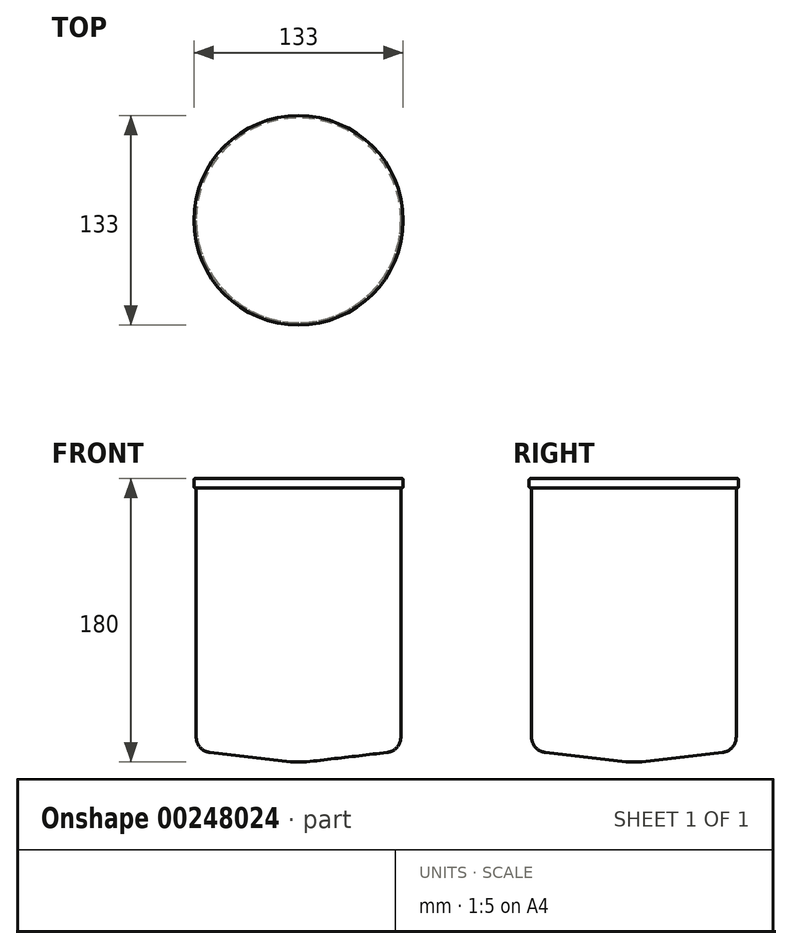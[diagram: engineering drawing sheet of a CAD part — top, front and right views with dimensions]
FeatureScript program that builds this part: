
annotation { "Feature Type Name" : "Feature", "Feature Type Description" : "" }
export const myFeature = defineFeature(function(context is Context, id is Id, definition is map)
    precondition{}
    {
        {
            var Q0;
            Q0=qCreatedBy(makeId("Top.planeOp"),FACE);
            var sketch = newSketch(context, id + "F0", { "sketchPlane" : qUnion([Q0])});
            skCircle(sketch, "E0", {"center": v(0, 0) * mm, "radius": 65 * mm});
            skSolve(sketch);
        }
        {
            var Q0;
            Q0=makeQuery(id+"F0.imprint","IMPRINT",FACE,{"disambiguationData":[TD([[makeQuery(id+"F0.imprint","IMPRINT",EDGE,{"derivedFrom":sQuery(id+"F0.wireOp",EDGE,"E0")}),1.0]])]});
            extrude(context, id + "F1", {"entities" : qUnion([Q0]), "oppositeDirection" : true, "depth" : 174 * mm, "offsetDistance" : 25 * mm});
        }
        {
            var Q0;
            Q0=makeQuery(id+"F1.opExtrude","CAP_EDGE",EDGE,{"disambiguationData":[OSD([sQuery(id+"F0.wireOp",EDGE,"E0")])],"isStart":false});
            chamfer(context, id + "F2", {"entities" : qUnion([Q0]), "chamferType" : ChamferType.TWO_OFFSETS, "width1" : 7 * mm, "oppositeDirection" : false, "width2" : 60 * mm, "tangentPropagation" : true});
        }
        {
            var Q0;
            {var subQ0=sQuery(id+"F0.wireOp",EDGE,"E0");Q0=makeQuery(id+"F2.opChamfer","BLEND_EDGE",EDGE,{"blendedFrom":[makeQuery(id+"F1.opExtrude","CAP_EDGE",EDGE,{"disambiguationData":[OSD([subQ0])],"isStart":false}),makeQuery(id+"F1.opExtrude","CAP_FACE",FACE,{"disambiguationData":[OSD([subQ0])],"isStart":false})],"blendedInto":[makeQuery(id+"F1.opExtrude","CAP_FACE",FACE,{"disambiguationData":[OSD([subQ0])],"isStart":false})]});}
            fillet(context, id + "F3", {"entities" : qUnion([Q0]), "radius" : 1 * mm, "tangentPropagation" : true, "allowEdgeOverflow" : false});
        }
        {
            var Q0;
            {var subQ0=sQuery(id+"F0.wireOp",EDGE,"E0");Q0=makeQuery(id+"F2.opChamfer","BLEND_EDGE",EDGE,{"blendedFrom":[makeQuery(id+"F1.opExtrude","CAP_EDGE",EDGE,{"disambiguationData":[OSD([subQ0])],"isStart":false}),makeQuery(id+"F1.opExtrude","SWEPT_FACE",FACE,{"disambiguationData":[OSD([subQ0])]})],"blendedInto":[makeQuery(id+"F1.opExtrude","SWEPT_FACE",FACE,{"disambiguationData":[OSD([subQ0])]})]});}
            fillet(context, id + "F4", {"entities" : qUnion([Q0]), "radius" : 10 * mm, "tangentPropagation" : true, "allowEdgeOverflow" : false});
        }
        {
            var Q0;
            Q0=makeQuery(id+"F1.opExtrude","CAP_FACE",FACE,{"disambiguationData":[OSD([sQuery(id+"F0.wireOp",EDGE,"E0")])],"isStart":true});
            var sketch = newSketch(context, id + "F5", { "sketchPlane" : qUnion([Q0])});
            skCircle(sketch, "E1", {"center": v(0, 0) * mm, "radius": 66.5 * mm});
            skSolve(sketch);
        }
        {
            var Q0;
            Q0=makeQuery(id+"F5.imprint","IMPRINT",FACE,{"disambiguationData":[TD([[makeQuery(id+"F5.imprint","IMPRINT",EDGE,{"derivedFrom":sQuery(id+"F5.wireOp",EDGE,"E1")}),1.0]])]});
            var Q1;
            Q1=makeQuery(id+"F5.imprint","IMPRINT",FACE,{"disambiguationData":[TD([[makeQuery(id+"F5.imprint","IMPRINT",EDGE,{"derivedFrom":makeQuery(id+"F1.opExtrude","CAP_EDGE",EDGE,{"disambiguationData":[OSD([sQuery(id+"F0.wireOp",EDGE,"E0")])],"isStart":true})}),1.0]])]});
            extrude(context, id + "F6", {"entities" : qUnion([Q0, Q1]), "operationType" : NewBodyOperationType.ADD, "depth" : 6 * mm, "offsetDistance" : 25 * mm});
        }
        {
            var Q0;
            Q0=makeQuery(id+"F6.opExtrude","CAP_EDGE",EDGE,{"disambiguationData":[OSD([sQuery(id+"F5.wireOp",EDGE,"E1")])],"isStart":false});
            var Q1;
            Q1=makeQuery(id+"F6.opExtrude","CAP_EDGE",EDGE,{"disambiguationData":[OSD([sQuery(id+"F5.wireOp",EDGE,"E1")])],"isStart":true});
            fillet(context, id + "F7", {"entities" : qUnion([Q0, Q1]), "radius" : 1 * mm, "tangentPropagation" : true, "allowEdgeOverflow" : false});
        }
    });
